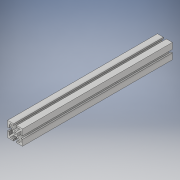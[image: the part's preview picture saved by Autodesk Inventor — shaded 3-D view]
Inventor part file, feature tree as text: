
AUTODESK INVENTOR PART (.ipt)
format: ipt  version: 2018 (Build 220112000, 112)  size: 154,112 bytes
history: native  units: mm
features: extrude x1, sketch x1
ambient origin geometry x8: Origin, YZ Plane, XZ Plane, XY Plane, X Axis, Y Axis, Z Axis, Center Point
bodies: Volumenkörper1 (feature_tree)
feature tree (2):
  extrude  "Extrusion1"  Depth=3.0mm
  sketch  "Skizze1"  dims[d0=3.0mm d1=3.0mm d2=0.5mm d3=1.0mm d4=1.0mm d5=1.2mm d6=1.2mm d7=1.2mm d8=1.2mm d9=0.3mm d10=0.15mm d11=0.15mm d12=0.15mm d13=0.15mm d14=30.0mm d15=0.0mm]
